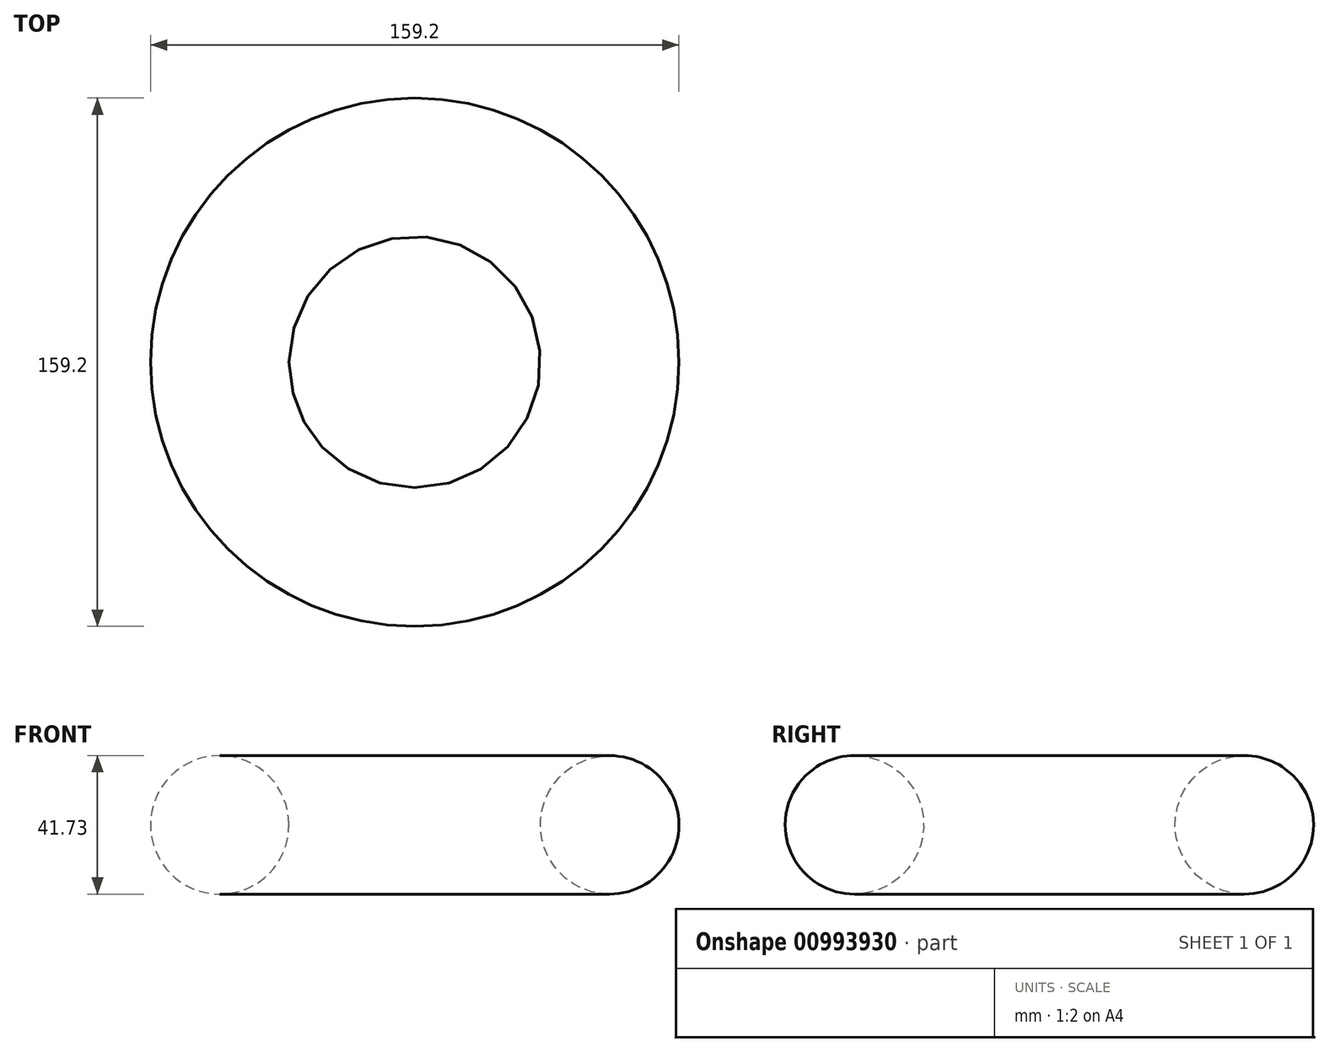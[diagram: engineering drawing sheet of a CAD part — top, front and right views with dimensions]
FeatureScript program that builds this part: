
annotation { "Feature Type Name" : "Feature", "Feature Type Description" : "" }
export const myFeature = defineFeature(function(context is Context, id is Id, definition is map)
    precondition{}
    {
        {
            var Q0;
            Q0=qCreatedBy(makeId("Right.planeOp"),FACE);
            var sketch = newSketch(context, id + "F0", { "sketchPlane" : qUnion([Q0])});
            skLineSegment(sketch, "E0", {"start": v(0, -70.45) * mm, "end": v(0, 0) * mm});
            skCircle(sketch, "E1", {"center": v(58.73, -55.8) * mm, "radius": 20.87 * mm});
            skSolve(sketch);
        }
        {
            var Q0;
            Q0=makeQuery(id+"F0.imprint","IMPRINT",FACE,{"disambiguationData":[TD([[makeQuery(id+"F0.imprint","IMPRINT",EDGE,{"derivedFrom":sQuery(id+"F0.wireOp",EDGE,"E1")}),1.0]])]});
            var Q1;
            Q1=sQuery(id+"F0.wireOp",EDGE,"E0");
            revolve(context, id + "F1", {"surfaceOperationType" : NewSurfaceOperationType.NEW, "entities" : qUnion([Q0]), "axis" : qUnion([Q1]), "revolveType" : RevolveType.FULL});
        }
    });
